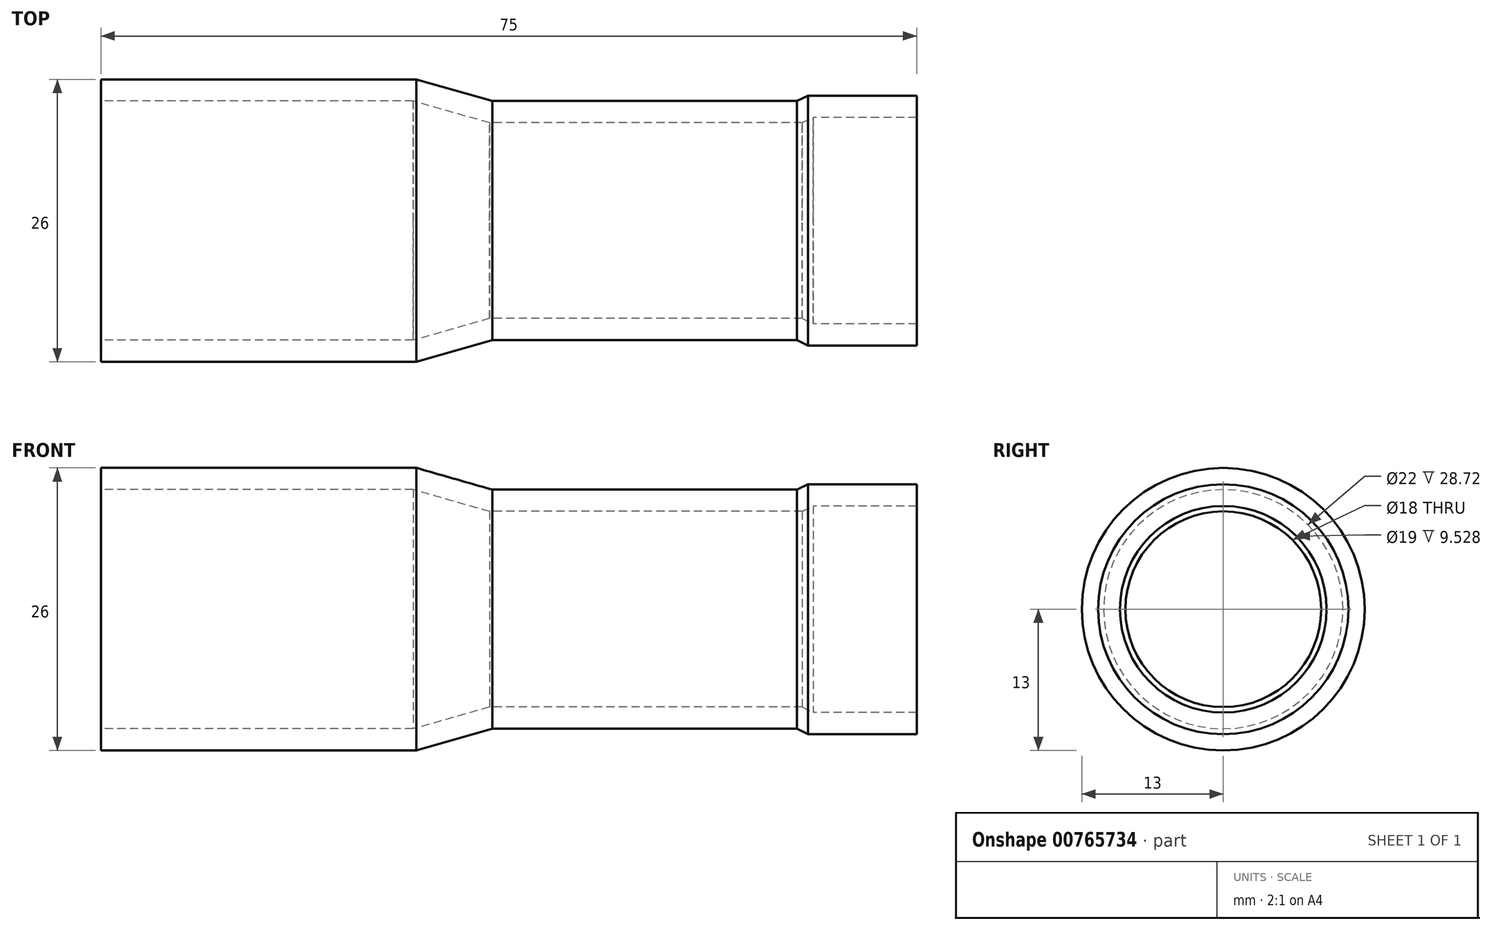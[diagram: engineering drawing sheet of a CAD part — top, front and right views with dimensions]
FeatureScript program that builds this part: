
annotation { "Feature Type Name" : "Feature", "Feature Type Description" : "" }
export const myFeature = defineFeature(function(context is Context, id is Id, definition is map)
    precondition{}
    {
        {
            var Q0;
            Q0=qCreatedBy(makeId("Front.planeOp"),FACE);
            var sketch = newSketch(context, id + "F0", { "sketchPlane" : qUnion([Q0])});
            skLineSegment(sketch, "E0", {"start": v(0, 11) * mm, "end": v(0, 13) * mm});
            skLineSegment(sketch, "E1", {"start": v(0, 13) * mm, "end": v(29, 13) * mm});
            skLineSegment(sketch, "E2", {"start": v(29, 13) * mm, "end": v(36, 11) * mm});
            skLineSegment(sketch, "E3", {"start": v(36, 11) * mm, "end": v(64, 11) * mm});
            skLineSegment(sketch, "E4", {"start": v(64, 11) * mm, "end": v(65, 11.5) * mm});
            skLineSegment(sketch, "E5", {"start": v(65, 11.5) * mm, "end": v(75, 11.5) * mm});
            skLineSegment(sketch, "E6", {"start": v(75, 11.5) * mm, "end": v(75, 9.5) * mm});
            skLineSegment(sketch, "E7", {"start": v(75, 0) * mm, "end": v(75, 0) * mm});
            skLineSegment(sketch, "E8", {"start": v(0, 0) * mm, "end": v(75, 0) * mm, "construction": true});
            skLineSegment(sketch, "E9.0", {"start": v(65.47, 9.5) * mm, "end": v(75, 9.5) * mm});
            skLineSegment(sketch, "E9.1", {"start": v(0, 11) * mm, "end": v(28.72, 11) * mm});
            skLineSegment(sketch, "E9.2", {"start": v(28.72, 11) * mm, "end": v(35.72, 9) * mm});
            skLineSegment(sketch, "E9.3", {"start": v(35.72, 9) * mm, "end": v(64.47, 9) * mm});
            skLineSegment(sketch, "E9.4", {"start": v(64.47, 9) * mm, "end": v(65.47, 9.5) * mm});
            skSolve(sketch);
        }
        {
            var Q0;
            Q0 = qSketchRegion(id + "F0", true);
            var Q1;
            Q1=sQuery(id+"F0.wireOp",EDGE,"E8");
            revolve(context, id + "F1", {"surfaceOperationType" : NewSurfaceOperationType.NEW, "entities" : qUnion([Q0]), "axis" : qUnion([Q1]), "revolveType" : RevolveType.FULL});
        }
    });
